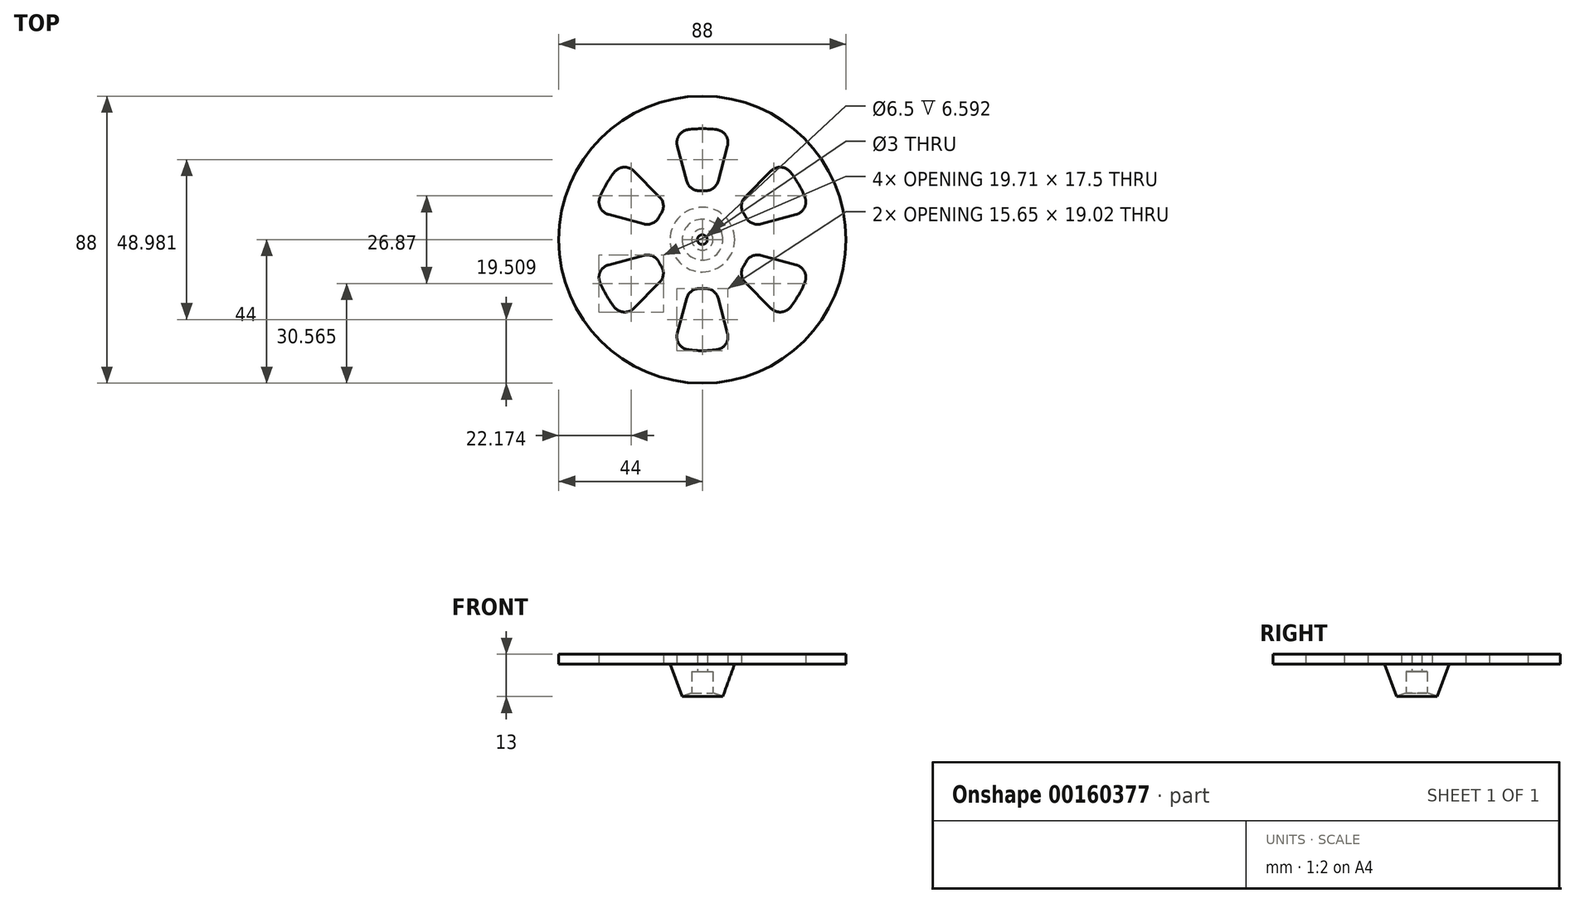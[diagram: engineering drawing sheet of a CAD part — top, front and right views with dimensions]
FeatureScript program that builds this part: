
annotation { "Feature Type Name" : "Feature", "Feature Type Description" : "" }
export const myFeature = defineFeature(function(context is Context, id is Id, definition is map)
    precondition{}
    {
        {
            var Q0;
            Q0=qCreatedBy(makeId("Top.planeOp"),FACE);
            var sketch = newSketch(context, id + "F0", { "sketchPlane" : qUnion([Q0])});
            skCircle(sketch, "E0", {"center": v(0, 0) * mm, "radius": 6.25 * mm});
            skSolve(sketch);
        }
        {
            var Q0;
            Q0=makeQuery(id+"F0.imprint","IMPRINT",FACE,{"disambiguationData":[TD([[makeQuery(id+"F0.imprint","IMPRINT",EDGE,{"derivedFrom":sQuery(id+"F0.wireOp",EDGE,"E0")}),1.0]])]});
            extrude(context, id + "F1", {"entities" : qUnion([Q0]), "depth" : 10 * mm, "hasDraft" : true, "draftAngle" : 20 * degree});
        }
        {
            var Q0;
            Q0=makeQuery(id+"F1.opExtrude","CAP_FACE",FACE,{"disambiguationData":[OSD([sQuery(id+"F0.wireOp",EDGE,"E0")])],"isStart":true});
            var sketch = newSketch(context, id + "F2", { "sketchPlane" : qUnion([Q0])});
            skCircle(sketch, "E1", {"center": v(0, 0) * mm, "radius": 3.25 * mm});
            skSolve(sketch);
        }
        {
            var Q0;
            Q0=makeQuery(id+"F2.imprint","IMPRINT",FACE,{"disambiguationData":[TD([[makeQuery(id+"F2.imprint","IMPRINT",EDGE,{"derivedFrom":sQuery(id+"F2.wireOp",EDGE,"E1")}),1.0]])]});
            extrude(context, id + "F3", {"entities" : qUnion([Q0]), "operationType" : NewBodyOperationType.REMOVE, "oppositeDirection" : true, "depth" : 7.6 * mm});
        }
        {
            var Q0;
            Q0=qCreatedBy(makeId("Front.planeOp"),FACE);
            var sketch = newSketch(context, id + "F4", { "sketchPlane" : qUnion([Q0])});
            skArc(sketch, "E2", {"start": v(0, 1.36) * mm, "mid": v(-3.2, 1.02) * mm, "end": v(-6.25, 0) * mm});
            skLineSegment(sketch, "E3.0", {"start": v(-6.25, 0) * mm, "end": v(0, 0) * mm});
            skLineSegment(sketch, "E4", {"start": v(0, 1.36) * mm, "end": v(0, -28.64) * mm, "construction": true});
            skPoint(sketch, "E5.orphan", {"position": v(6.25, 0) * mm});
            skLineSegment(sketch, "E6", {"start": v(0, 1.36) * mm, "end": v(0, 0) * mm});
            skSolve(sketch);
        }
        {
            var Q0;
            Q0 = qSketchRegion(id + "F4", true);
            var Q1;
            Q1=sQuery(id+"F4.wireOp",EDGE,"E4");
            revolve(context, id + "F5", {"operationType" : NewBodyOperationType.REMOVE, "entities" : qUnion([Q0]), "axis" : qUnion([Q1]), "revolveType" : RevolveType.FULL, "oppositeDirection" : true});
        }
        {
            var Q0;
            Q0=makeQuery(id+"F1.opExtrude","CAP_FACE",FACE,{"disambiguationData":[OSD([sQuery(id+"F0.wireOp",EDGE,"E0")])],"isStart":false});
            var sketch = newSketch(context, id + "F6", { "sketchPlane" : qUnion([Q0])});
            skCircle(sketch, "E7", {"center": v(0, 0) * mm, "radius": 44 * mm});
            skLineSegment(sketch, "E8", {"start": v(0, 0) * mm, "end": v(0, 44) * mm, "construction": true});
            skLineSegment(sketch, "E9", {"start": v(-3.88, 14.49) * mm, "end": v(-8.8, 32.84) * mm});
            skLineSegment(sketch, "E10", {"start": v(3.88, 14.49) * mm, "end": v(8.8, 32.84) * mm});
            skArc(sketch, "E11", {"start": v(8.8, 32.84) * mm, "mid": v(0, 34) * mm, "end": v(-8.8, 32.84) * mm});
            skArc(sketch, "E12", {"start": v(3.88, 14.49) * mm, "mid": v(0, 15) * mm, "end": v(-3.88, 14.49) * mm});
            skArc(sketch, "E13.1.0", {"start": v(-10.6, 10.6) * mm, "mid": v(-13, 7.5) * mm, "end": v(-14.49, 3.88) * mm});
            skLineSegment(sketch, "E13.1.1", {"start": v(-10.6, 10.6) * mm, "end": v(-24.04, 24.04) * mm});
            skArc(sketch, "E13.1.2", {"start": v(-24.04, 24.04) * mm, "mid": v(-29.44, 17) * mm, "end": v(-32.84, 8.8) * mm});
            skLineSegment(sketch, "E13.1.3", {"start": v(-14.49, 3.88) * mm, "end": v(-32.84, 8.8) * mm});
            skArc(sketch, "E13.2.0", {"start": v(-14.49, -3.88) * mm, "mid": v(-13, -7.5) * mm, "end": v(-10.6, -10.6) * mm});
            skLineSegment(sketch, "E13.2.1", {"start": v(-14.49, -3.88) * mm, "end": v(-32.84, -8.8) * mm});
            skArc(sketch, "E13.2.2", {"start": v(-32.84, -8.8) * mm, "mid": v(-29.44, -17) * mm, "end": v(-24.04, -24.04) * mm});
            skLineSegment(sketch, "E13.2.3", {"start": v(-10.6, -10.6) * mm, "end": v(-24.04, -24.04) * mm});
            skArc(sketch, "E14.1.3.0", {"start": v(-3.88, -14.49) * mm, "mid": v(0, -15) * mm, "end": v(3.88, -14.49) * mm});
            skLineSegment(sketch, "E14.4.3.0", {"start": v(-3.88, -14.49) * mm, "end": v(-8.8, -32.84) * mm});
            skArc(sketch, "E14.7.3.0", {"start": v(-8.8, -32.84) * mm, "mid": v(0, -34) * mm, "end": v(8.8, -32.84) * mm});
            skLineSegment(sketch, "E14.11.3.0", {"start": v(3.88, -14.49) * mm, "end": v(8.8, -32.84) * mm});
            skArc(sketch, "E14.1.4.0", {"start": v(10.6, -10.6) * mm, "mid": v(13, -7.5) * mm, "end": v(14.49, -3.88) * mm});
            skLineSegment(sketch, "E14.4.4.0", {"start": v(10.6, -10.6) * mm, "end": v(24.04, -24.04) * mm});
            skArc(sketch, "E14.7.4.0", {"start": v(24.04, -24.04) * mm, "mid": v(29.44, -17) * mm, "end": v(32.84, -8.8) * mm});
            skLineSegment(sketch, "E14.11.4.0", {"start": v(14.49, -3.88) * mm, "end": v(32.84, -8.8) * mm});
            skArc(sketch, "E14.1.5.0", {"start": v(14.49, 3.88) * mm, "mid": v(13, 7.5) * mm, "end": v(10.6, 10.6) * mm});
            skLineSegment(sketch, "E14.4.5.0", {"start": v(14.49, 3.88) * mm, "end": v(32.84, 8.8) * mm});
            skArc(sketch, "E14.7.5.0", {"start": v(32.84, 8.8) * mm, "mid": v(29.44, 17) * mm, "end": v(24.04, 24.04) * mm});
            skLineSegment(sketch, "E14.11.5.0", {"start": v(10.6, 10.6) * mm, "end": v(24.04, 24.04) * mm});
            skCircle(sketch, "E15", {"center": v(0, 0) * mm, "radius": 1.5 * mm});
            skSolve(sketch);
        }
        {
            var Q0;
            Q0=makeQuery(id+"F6.imprint","IMPRINT",FACE,{"disambiguationData":[TD([[makeQuery(id+"F6.imprint","IMPRINT",EDGE,{"derivedFrom":sQuery(id+"F6.wireOp",EDGE,"E7")}),1.0]])]});
            var Q1;
            Q1=makeQuery(id+"F6.imprint","IMPRINT",FACE,{"disambiguationData":[TD([[makeQuery(id+"F6.imprint","IMPRINT",EDGE,{"derivedFrom":makeQuery(id+"F1.opExtrude","CAP_EDGE",EDGE,{"disambiguationData":[OSD([sQuery(id+"F0.wireOp",EDGE,"E0")])],"isStart":false})}),1.0]])]});
            extrude(context, id + "F7", {"entities" : qUnion([Q0, Q1]), "operationType" : NewBodyOperationType.ADD, "depth" : 3 * mm});
        }
        {
            var Q0;
            Q0=makeQuery(id+"F1.opExtrude","CAP_EDGE",EDGE,{"disambiguationData":[OSD([sQuery(id+"F0.wireOp",EDGE,"E0")])],"isStart":false});
            var Q1;
            Q1=makeQuery(id+"F7.opExtrude","SWEPT_EDGE",EDGE,{"disambiguationData":[OSD([sQuery(id+"F6.wireOp",EDGE,"E13.2.0"),sQuery(id+"F6.wireOp",EDGE,"E13.2.3")])]});
            var Q2;
            Q2=makeQuery(id+"F7.opExtrude","SWEPT_EDGE",EDGE,{"disambiguationData":[OSD([sQuery(id+"F6.wireOp",EDGE,"E13.2.0"),sQuery(id+"F6.wireOp",EDGE,"E13.2.1")])]});
            var Q3;
            Q3=makeQuery(id+"F7.opExtrude","SWEPT_EDGE",EDGE,{"disambiguationData":[OSD([sQuery(id+"F6.wireOp",EDGE,"E13.2.1"),sQuery(id+"F6.wireOp",EDGE,"E13.2.2")])]});
            var Q4;
            Q4=makeQuery(id+"F7.opExtrude","SWEPT_EDGE",EDGE,{"disambiguationData":[OSD([sQuery(id+"F6.wireOp",EDGE,"E13.2.2"),sQuery(id+"F6.wireOp",EDGE,"E13.2.3")])]});
            var Q5;
            Q5=makeQuery(id+"F7.opExtrude","SWEPT_EDGE",EDGE,{"disambiguationData":[OSD([sQuery(id+"F6.wireOp",EDGE,"E14.7.3.0"),sQuery(id+"F6.wireOp",EDGE,"E14.11.3.0")])]});
            var Q6;
            Q6=makeQuery(id+"F7.opExtrude","SWEPT_EDGE",EDGE,{"disambiguationData":[OSD([sQuery(id+"F6.wireOp",EDGE,"E14.1.3.0"),sQuery(id+"F6.wireOp",EDGE,"E14.11.3.0")])]});
            var Q7;
            Q7=makeQuery(id+"F7.opExtrude","SWEPT_EDGE",EDGE,{"disambiguationData":[OSD([sQuery(id+"F6.wireOp",EDGE,"E9"),sQuery(id+"F6.wireOp",EDGE,"E11")])]});
            var Q8;
            Q8=makeQuery(id+"F7.opExtrude","SWEPT_EDGE",EDGE,{"disambiguationData":[OSD([sQuery(id+"F6.wireOp",EDGE,"E13.1.1"),sQuery(id+"F6.wireOp",EDGE,"E13.1.2")])]});
            var Q9;
            Q9=makeQuery(id+"F7.opExtrude","SWEPT_EDGE",EDGE,{"disambiguationData":[OSD([sQuery(id+"F6.wireOp",EDGE,"E13.1.0"),sQuery(id+"F6.wireOp",EDGE,"E13.1.1")])]});
            var Q10;
            Q10=makeQuery(id+"F7.opExtrude","SWEPT_EDGE",EDGE,{"disambiguationData":[OSD([sQuery(id+"F6.wireOp",EDGE,"E14.7.4.0"),sQuery(id+"F6.wireOp",EDGE,"E14.11.4.0")])]});
            var Q11;
            Q11=makeQuery(id+"F7.opExtrude","SWEPT_EDGE",EDGE,{"disambiguationData":[OSD([sQuery(id+"F6.wireOp",EDGE,"E14.1.4.0"),sQuery(id+"F6.wireOp",EDGE,"E14.11.4.0")])]});
            var Q12;
            Q12=makeQuery(id+"F7.opExtrude","SWEPT_EDGE",EDGE,{"disambiguationData":[OSD([sQuery(id+"F6.wireOp",EDGE,"E14.1.5.0"),sQuery(id+"F6.wireOp",EDGE,"E14.11.5.0")])]});
            var Q13;
            Q13=makeQuery(id+"F7.opExtrude","SWEPT_EDGE",EDGE,{"disambiguationData":[OSD([sQuery(id+"F6.wireOp",EDGE,"E14.1.3.0"),sQuery(id+"F6.wireOp",EDGE,"E14.4.3.0")])]});
            var Q14;
            Q14=makeQuery(id+"F7.opExtrude","SWEPT_EDGE",EDGE,{"disambiguationData":[OSD([sQuery(id+"F6.wireOp",EDGE,"E14.1.4.0"),sQuery(id+"F6.wireOp",EDGE,"E14.4.4.0")])]});
            var Q15;
            Q15=makeQuery(id+"F7.opExtrude","SWEPT_EDGE",EDGE,{"disambiguationData":[OSD([sQuery(id+"F6.wireOp",EDGE,"E14.4.4.0"),sQuery(id+"F6.wireOp",EDGE,"E14.7.4.0")])]});
            var Q16;
            Q16=makeQuery(id+"F7.opExtrude","SWEPT_EDGE",EDGE,{"disambiguationData":[OSD([sQuery(id+"F6.wireOp",EDGE,"E14.4.5.0"),sQuery(id+"F6.wireOp",EDGE,"E14.7.5.0")])]});
            var Q17;
            Q17=makeQuery(id+"F7.opExtrude","SWEPT_EDGE",EDGE,{"disambiguationData":[OSD([sQuery(id+"F6.wireOp",EDGE,"E14.1.5.0"),sQuery(id+"F6.wireOp",EDGE,"E14.4.5.0")])]});
            var Q18;
            Q18=makeQuery(id+"F7.opExtrude","SWEPT_EDGE",EDGE,{"disambiguationData":[OSD([sQuery(id+"F6.wireOp",EDGE,"E10"),sQuery(id+"F6.wireOp",EDGE,"E12")])]});
            var Q19;
            Q19=makeQuery(id+"F7.opExtrude","SWEPT_EDGE",EDGE,{"disambiguationData":[OSD([sQuery(id+"F6.wireOp",EDGE,"E14.4.3.0"),sQuery(id+"F6.wireOp",EDGE,"E14.7.3.0")])]});
            var Q20;
            Q20=makeQuery(id+"F7.opExtrude","SWEPT_EDGE",EDGE,{"disambiguationData":[OSD([sQuery(id+"F6.wireOp",EDGE,"E13.1.2"),sQuery(id+"F6.wireOp",EDGE,"E13.1.3")])]});
            var Q21;
            Q21=makeQuery(id+"F7.opExtrude","SWEPT_EDGE",EDGE,{"disambiguationData":[OSD([sQuery(id+"F6.wireOp",EDGE,"E13.1.0"),sQuery(id+"F6.wireOp",EDGE,"E13.1.3")])]});
            var Q22;
            Q22=makeQuery(id+"F7.opExtrude","SWEPT_EDGE",EDGE,{"disambiguationData":[OSD([sQuery(id+"F6.wireOp",EDGE,"E9"),sQuery(id+"F6.wireOp",EDGE,"E12")])]});
            var Q23;
            Q23=makeQuery(id+"F7.opExtrude","SWEPT_EDGE",EDGE,{"disambiguationData":[OSD([sQuery(id+"F6.wireOp",EDGE,"E10"),sQuery(id+"F6.wireOp",EDGE,"E11")])]});
            var Q24;
            Q24=makeQuery(id+"F7.opExtrude","SWEPT_EDGE",EDGE,{"disambiguationData":[OSD([sQuery(id+"F6.wireOp",EDGE,"E14.7.5.0"),sQuery(id+"F6.wireOp",EDGE,"E14.11.5.0")])]});
            fillet(context, id + "F8", {"entities" : qUnion([Q0, Q1, Q2, Q3, Q4, Q5, Q6, Q7, Q8, Q9, Q10, Q11, Q12, Q13, Q14, Q15, Q16, Q17, Q18, Q19, Q20, Q21, Q22, Q23, Q24]), "radius" : 4 * mm, "tangentPropagation" : true, "allowEdgeOverflow" : false});
        }
        {
            var Q0;
            Q0=makeQuery(id+"F1.opExtrude","CAP_FACE",FACE,{"disambiguationData":[OSD([sQuery(id+"F0.wireOp",EDGE,"E0")])],"isStart":false});
            extrude(context, id + "F9", {"entities" : qUnion([Q0]), "operationType" : NewBodyOperationType.REMOVE, "oppositeDirection" : true, "depth" : 25 * mm});
        }
    });
